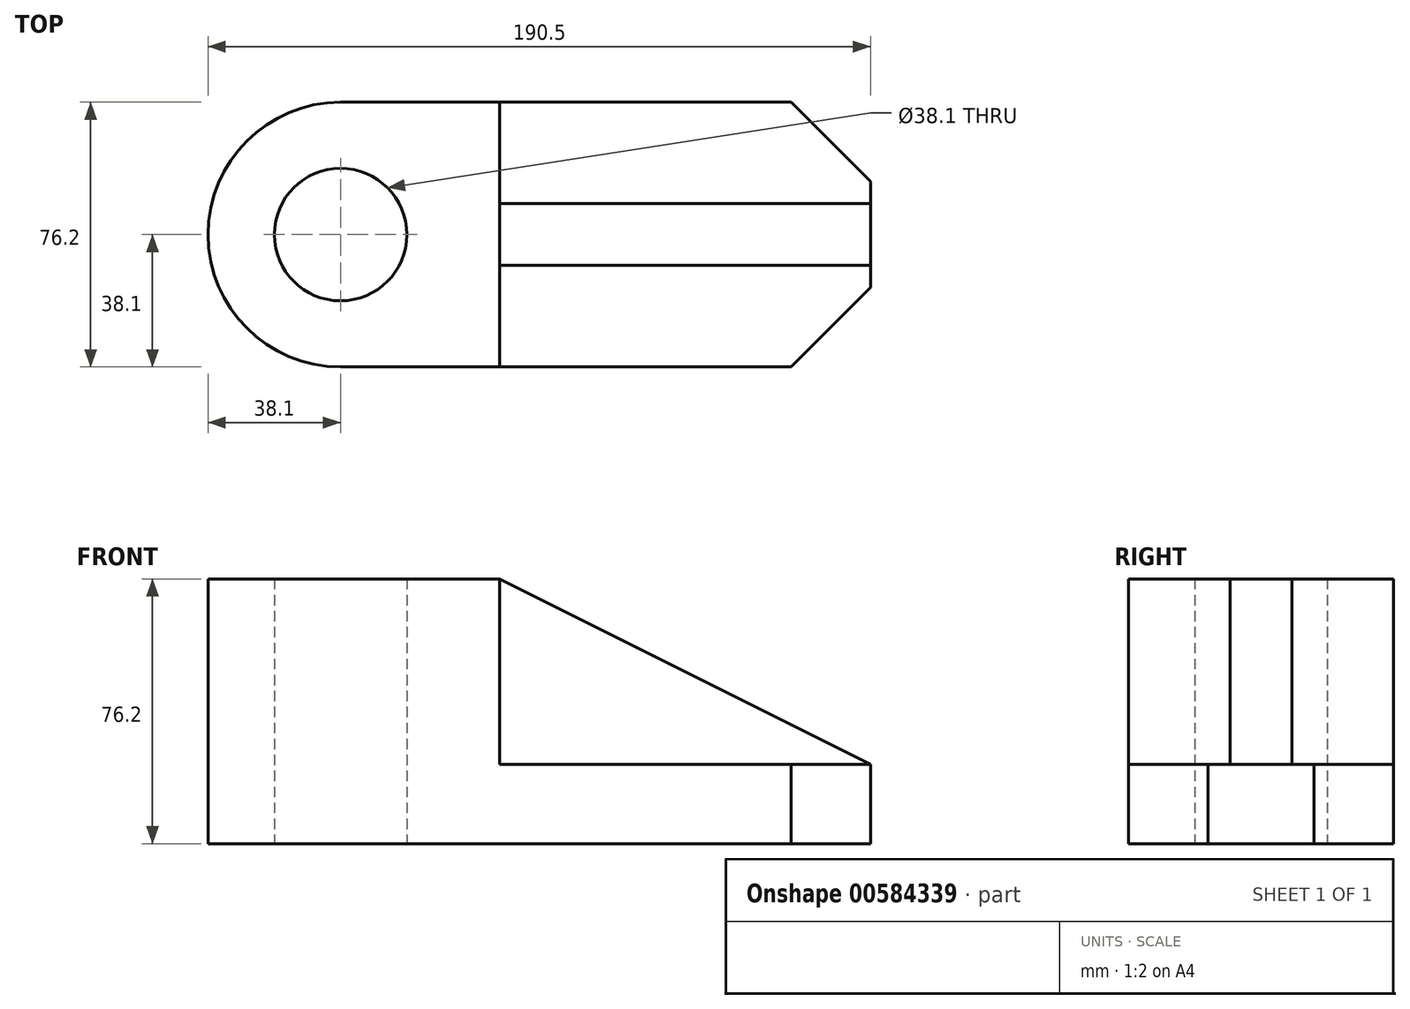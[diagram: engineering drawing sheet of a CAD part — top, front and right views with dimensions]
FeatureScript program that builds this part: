
annotation { "Feature Type Name" : "Feature", "Feature Type Description" : "" }
export const myFeature = defineFeature(function(context is Context, id is Id, definition is map)
    precondition{}
    {
        {
            var Q0;
            Q0=qCreatedBy(makeId("Top.planeOp"),FACE);
            var sketch = newSketch(context, id + "F0", { "sketchPlane" : qUnion([Q0])});
            skArc(sketch, "E0", {"start": v(0, 38.1) * mm, "mid": v(-38.1, 0) * mm, "end": v(0, -38.1) * mm});
            skCircle(sketch, "E1", {"center": v(0, 0) * mm, "radius": 19.05 * mm});
            skLineSegment(sketch, "E2", {"start": v(0, -38.1) * mm, "end": v(129.54, -38.1) * mm});
            skLineSegment(sketch, "E3", {"start": v(0, 38.1) * mm, "end": v(129.54, 38.1) * mm});
            skLineSegment(sketch, "E4", {"start": v(152.4, 15.24) * mm, "end": v(152.4, -15.24) * mm});
            skLineSegment(sketch, "E5", {"start": v(45.72, 38.1) * mm, "end": v(45.72, -38.1) * mm});
            skLineSegment(sketch, "E6", {"start": v(129.54, -38.1) * mm, "end": v(152.4, -15.24) * mm});
            skLineSegment(sketch, "E7", {"start": v(129.54, 38.1) * mm, "end": v(152.4, 15.24) * mm});
            skLineSegment(sketch, "E8", {"start": v(152.4, 8.89) * mm, "end": v(45.72, 8.89) * mm});
            skPoint(sketch, "E8.endSnap0", {"position": v(45.72, 0) * mm});
            skLineSegment(sketch, "E9", {"start": v(152.4, -8.9) * mm, "end": v(45.72, -8.9) * mm});
            skPoint(sketch, "E10.orphan", {"position": v(152.4, 38.1) * mm});
            skSolve(sketch);
        }
        {
            var Q0;
            {var subQ1=sQuery(id+"F0.wireOp",EDGE,"E0");Q0=makeQuery(id+"F0.imprint","IMPRINT",FACE,{"disambiguationData":[TD([[makeQuery(id+"F0.imprint","IMPRINT",EDGE,{"derivedFrom":subQ1}),1.0]])]});}
            extrude(context, id + "F1", {"entities" : qUnion([Q0]), "depth" : 76.2 * mm, "offsetDistance" : 25.4 * mm});
        }
        {
            var Q0;
            {var subQ0=sQuery(id+"F0.wireOp",EDGE,"E6");Q0=makeQuery(id+"F0.imprint","IMPRINT",FACE,{"disambiguationData":[TD([[makeQuery(id+"F0.imprint","IMPRINT",EDGE,{"derivedFrom":subQ0}),1.0]])]});}
            extrude(context, id + "F2", {"entities" : qUnion([Q0]), "operationType" : NewBodyOperationType.ADD, "depth" : 22.86 * mm, "offsetDistance" : 25.4 * mm});
        }
        {
            var Q0;
            {var subQ0=sQuery(id+"F0.wireOp",EDGE,"E7");Q0=makeQuery(id+"F0.imprint","IMPRINT",FACE,{"disambiguationData":[TD([[makeQuery(id+"F0.imprint","IMPRINT",EDGE,{"derivedFrom":subQ0}),-1.0]])]});}
            extrude(context, id + "F3", {"entities" : qUnion([Q0]), "operationType" : NewBodyOperationType.ADD, "depth" : 22.86 * mm, "offsetDistance" : 25.4 * mm});
        }
        {
            var Q0;
            {var subQ0=sQuery(id+"F0.wireOp",EDGE,"E8");Q0=makeQuery(id+"F0.imprint","IMPRINT",FACE,{"disambiguationData":[TD([[makeQuery(id+"F0.imprint","IMPRINT",EDGE,{"derivedFrom":subQ0}),1.0]])]});}
            extrude(context, id + "F4", {"entities" : qUnion([Q0]), "operationType" : NewBodyOperationType.ADD, "depth" : 76.2 * mm, "offsetDistance" : 25.4 * mm});
        }
        {
            var Q0;
            Q0=makeQuery(id+"F4.opExtrude","SWEPT_FACE",FACE,{"disambiguationData":[OSD([sQuery(id+"F0.wireOp",EDGE,"E9")])]});
            var sketch = newSketch(context, id + "F5", { "sketchPlane" : qUnion([Q0])});
            skLineSegment(sketch, "E11", {"start": v(45.72, 76.2) * mm, "end": v(152.4, 22.86) * mm});
            skSolve(sketch);
        }
        {
            var Q0;
            Q0=makeQuery(id+"F5.imprint","IMPRINT",FACE,{"disambiguationData":[TD([[makeQuery(id+"F5.imprint","IMPRINT",EDGE,{"derivedFrom":sQuery(id+"F5.wireOp",EDGE,"E11")}),1.0]])]});
            extrude(context, id + "F6", {"entities" : qUnion([Q0]), "operationType" : NewBodyOperationType.REMOVE, "oppositeDirection" : true, "depth" : 25.4 * mm, "offsetDistance" : 25.4 * mm});
        }
    });
